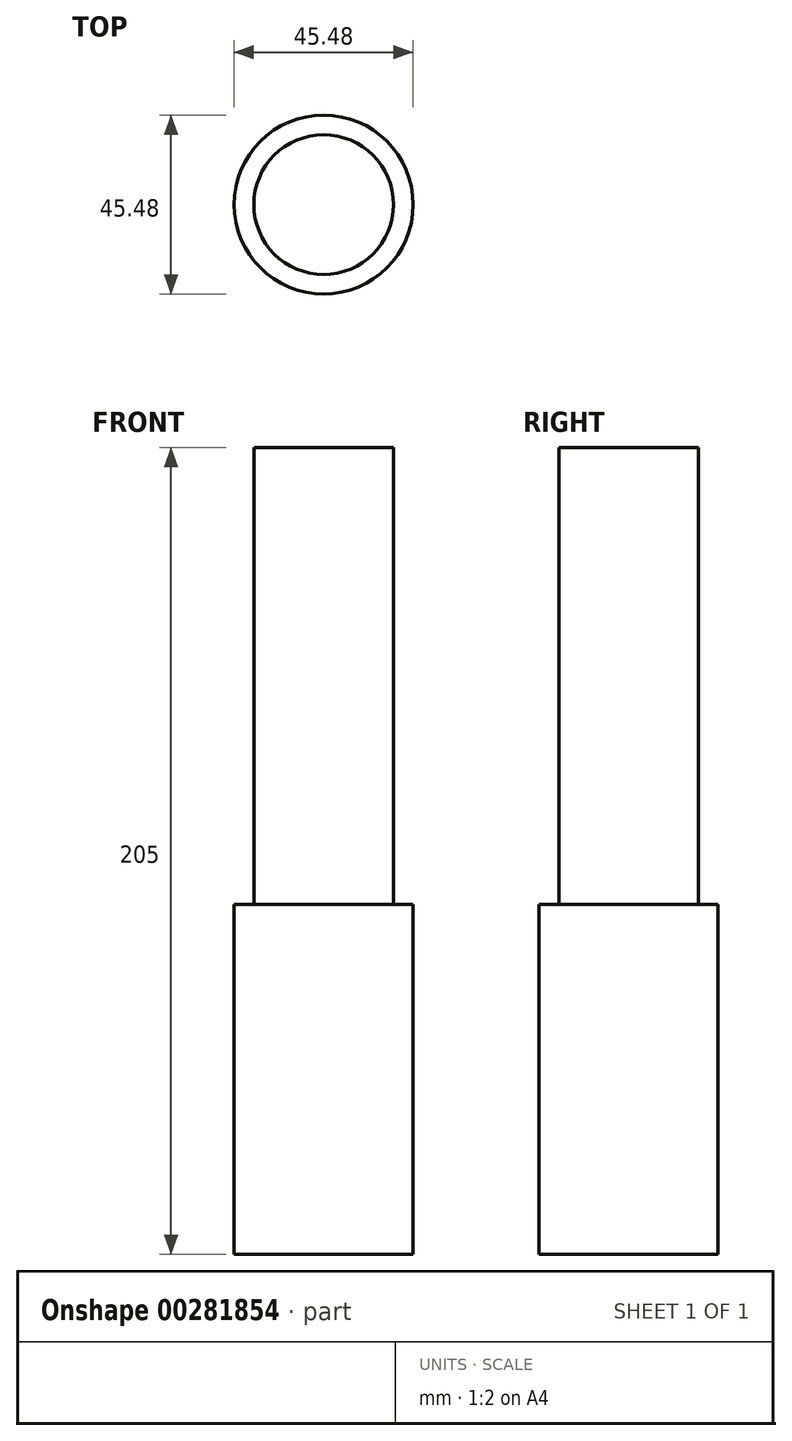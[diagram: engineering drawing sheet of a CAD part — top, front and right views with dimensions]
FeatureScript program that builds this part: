
annotation { "Feature Type Name" : "Feature", "Feature Type Description" : "" }
export const myFeature = defineFeature(function(context is Context, id is Id, definition is map)
    precondition{}
    {
        {
            var Q0;
            Q0=qCreatedBy(makeId("Front.planeOp"),FACE);
            var sketch = newSketch(context, id + "F0", { "sketchPlane" : qUnion([Q0])});
            skLineSegment(sketch, "E0.bottom", {"start": v(22.74, -44.45) * mm, "end": v(-22.74, -44.45) * mm});
            skLineSegment(sketch, "E0.top", {"start": v(22.74, 44.45) * mm, "end": v(-22.74, 44.45) * mm});
            skLineSegment(sketch, "E0.left", {"start": v(22.74, -44.45) * mm, "end": v(22.74, 44.45) * mm});
            skLineSegment(sketch, "E0.right", {"start": v(-22.74, -44.45) * mm, "end": v(-22.74, 44.45) * mm});
            skPoint(sketch, "E0.middle", {"position": v(0, 0) * mm});
            skLineSegment(sketch, "E1", {"start": v(0, 44.45) * mm, "end": v(0, -44.45) * mm});
            skSolve(sketch);
        }
        {
            var Q0;
            {var subQ0=sQuery(id+"F0.wireOp",EDGE,"E0.right");Q0=makeQuery(id+"F0.imprint","IMPRINT",FACE,{"disambiguationData":[TD([[makeQuery(id+"F0.imprint","IMPRINT",EDGE,{"derivedFrom":subQ0}),-1.0]])]});}
            var Q1;
            Q1=sQuery(id+"F0.wireOp",EDGE,"E1");
            revolve(context, id + "F1", {"entities" : qUnion([Q0]), "axis" : qUnion([Q1]), "revolveType" : RevolveType.FULL, "oppositeDirection" : true});
        }
        {
            var Q0;
            Q0=makeQuery(id+"F1.opRevolve","SWEPT_FACE",FACE,{"disambiguationData":[OSD([sQuery(id+"F0.wireOp",EDGE,"E0.top")])]});
            shell(context, id + "F2", {"entities" : qUnion([Q0]), "thickness" : 5 * mm});
        }
        {
            var Q0;
            Q0=makeQuery(id+"F2.opShell","OFFSET_FACE",FACE,{"disambiguationData":[OSD([sQuery(id+"F0.wireOp",EDGE,"E0.bottom")])]});
            extrude(context, id + "F3", {"entities" : qUnion([Q0]), "operationType" : NewBodyOperationType.ADD, "depth" : 200 * mm});
        }
    });
